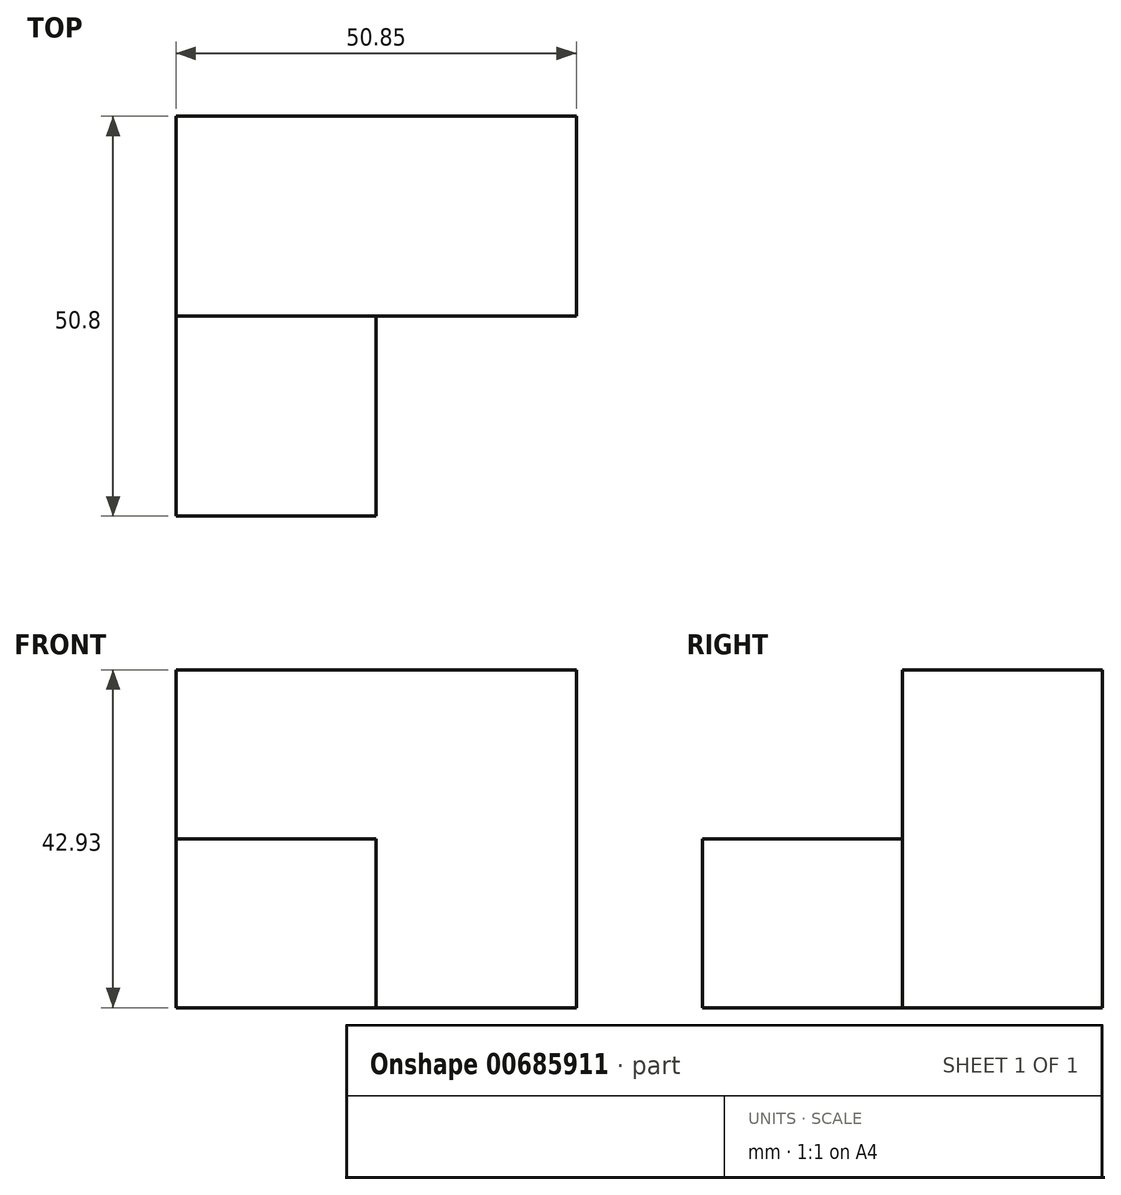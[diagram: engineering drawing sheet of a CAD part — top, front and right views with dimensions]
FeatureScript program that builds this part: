
annotation { "Feature Type Name" : "Feature", "Feature Type Description" : "" }
export const myFeature = defineFeature(function(context is Context, id is Id, definition is map)
    precondition{}
    {
        {
            var Q0;
            Q0=qCreatedBy(makeId("Front.planeOp"),FACE);
            var sketch = newSketch(context, id + "F0", { "sketchPlane" : qUnion([Q0])});
            skLineSegment(sketch, "E0.bottom", {"start": v(0, 31.53) * mm, "end": v(-50.85, 31.53) * mm});
            skLineSegment(sketch, "E0.top", {"start": v(0, -11.4) * mm, "end": v(-50.85, -11.4) * mm});
            skLineSegment(sketch, "E0.left", {"start": v(0, 31.53) * mm, "end": v(0, -11.4) * mm});
            skLineSegment(sketch, "E0.right", {"start": v(-50.85, 31.53) * mm, "end": v(-50.85, -11.4) * mm});
            skSolve(sketch);
        }
        {
            var Q0;
            Q0=makeQuery(id+"F0.imprint","IMPRINT",FACE,{"disambiguationData":[TD([[makeQuery(id+"F0.imprint","IMPRINT",EDGE,{"derivedFrom":sQuery(id+"F0.wireOp",EDGE,"E0.bottom")}),1.0]])]});
            extrude(context, id + "F1", {"entities" : qUnion([Q0]), "depth" : 25.4 * mm, "offsetDistance" : 25.4 * mm});
        }
        {
            var Q0;
            Q0=makeQuery(id+"F1.opExtrude","CAP_FACE",FACE,{"disambiguationData":[OSD([sQuery(id+"F0.wireOp",EDGE,"E0.bottom"),sQuery(id+"F0.wireOp",EDGE,"E0.top"),sQuery(id+"F0.wireOp",EDGE,"E0.left"),sQuery(id+"F0.wireOp",EDGE,"E0.right")])],"isStart":false});
            var sketch = newSketch(context, id + "F2", { "sketchPlane" : qUnion([Q0])});
            skLineSegment(sketch, "E1", {"start": v(-50.85, 10.06) * mm, "end": v(-25.45, 10.06) * mm});
            skLineSegment(sketch, "E2", {"start": v(-25.45, 10.06) * mm, "end": v(-25.45, -11.4) * mm});
            skLineSegment(sketch, "E3", {"start": v(-25.45, -11.4) * mm, "end": v(-50.85, -11.4) * mm});
            skLineSegment(sketch, "E4", {"start": v(-50.85, -11.4) * mm, "end": v(-50.85, 10.06) * mm});
            skSolve(sketch);
        }
        {
            var Q0;
            Q0 = qSketchRegion(id + "F2", true);
            extrude(context, id + "F3", {"entities" : qUnion([Q0]), "operationType" : NewBodyOperationType.ADD, "depth" : 25.4 * mm, "offsetDistance" : 25.4 * mm});
        }
    });
